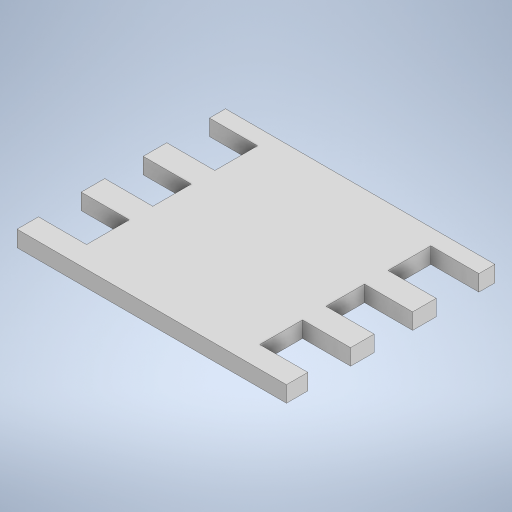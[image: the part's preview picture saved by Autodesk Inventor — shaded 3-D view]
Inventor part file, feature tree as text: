
AUTODESK INVENTOR PART (.ipt)
format: ipt  version: 2024 (Build 280153000, 153)  size: 278,528 bytes
history: native  units: mm
features: extrude x2, sketch x2
ambient origin geometry x8: Origin, YZ Plane, XZ Plane, XY Plane, X Axis, Y Axis, Z Axis, Center Point
bodies: Solid1 (feature_tree)
feature tree (4):
  extrude  "Extrusion1"  Depth=160.0mm
  extrude  "Extrusion3"  Depth=40.0mm
  sketch  "Sketch1"  dims[d0=162.0mm d1=160.0mm]
  sketch  "Sketch4"  dims[d2=40.0mm d5=40.0mm d7=45.0mm d8=45.0mm d9=20.0mm d10=45.0mm d11=15.0mm d12=45.0mm d13=207.0mm d14=15.0mm d15=15.0mm d16=0.0mm d25=36.0mm d26=22.0mm d27=0.0mm d28=0.0mm d29=22.0mm d30=15.0mm d31=0.0mm d32=0.0mm d33=45.0mm d34=45.0mm d35=45.0mm d36=36.0mm d37=22.0mm d38=22.0mm]
